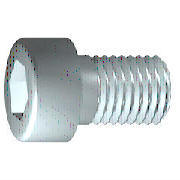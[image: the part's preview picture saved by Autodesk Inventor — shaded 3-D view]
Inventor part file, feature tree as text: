
AUTODESK INVENTOR PART (.ipt)
format: ipt  version: 2019 (Build 230136000, 136)  size: 194,048 bytes
history: native  units: mm (DEFAULTED — no unit token found)
features: sketch x2, extrude x1, plane x1, fillet x1
ambient origin geometry x7: Origin, YZ Plane, XY Plane, X Axis, Y Axis, Z Axis, Center Point
bodies: Solid1 (feature_tree), Body (feature_tree)
feature tree (5):
  extrude  "Slot"  Depth=6.0mm
  plane  "Work Plane1"
  fillet  "Fillet2"  Radius=6.0mm
  sketch  "Sketch1"  dims[d1=22.5mm d2=0.61355mm d3=6.0mm]
  sketch  "Sketch2"  dims[d4=3.0mm d5=60.0deg d6=6.0mm d7=6.0mm d8=5.773503mm d9=10.0mm d10=90.0deg d11=10.0mm d12=0.0mm d13=22.5mm d14=0.0mm d15=0.61345mm d16=0.61345mm d17=0.6mm d19=0.0mm d26=25.0mm d27=45.0deg d28=0.0mm d29=0.0mm d30=0.1mm]
